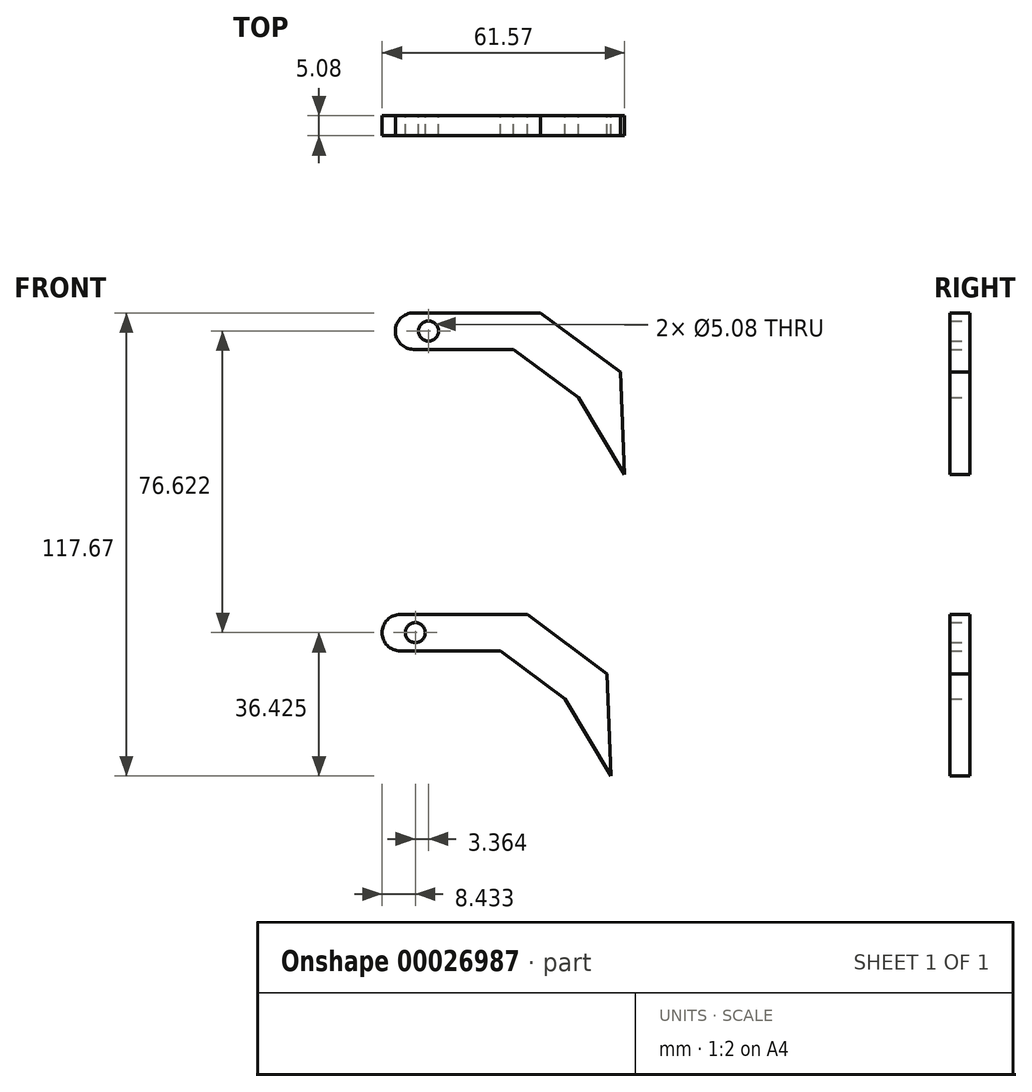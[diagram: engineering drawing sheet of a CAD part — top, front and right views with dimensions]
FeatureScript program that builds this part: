
annotation { "Feature Type Name" : "Feature", "Feature Type Description" : "" }
export const myFeature = defineFeature(function(context is Context, id is Id, definition is map)
    precondition{}
    {
        {
            var Q0;
            Q0=qCreatedBy(makeId("Front.planeOp"),FACE);
            var sketch = newSketch(context, id + "F0", { "sketchPlane" : qUnion([Q0])});
            skLineSegment(sketch, "E0.bottom", {"start": v(-41.86, 34.1) * mm, "end": v(-16.46, 34.1) * mm});
            skLineSegment(sketch, "E0.top", {"start": v(-41.86, 24.85) * mm, "end": v(-16.46, 24.85) * mm});
            skLineSegment(sketch, "E0.left", {"start": v(-41.86, 34.1) * mm, "end": v(-41.86, 24.85) * mm});
            skLineSegment(sketch, "E0.right", {"start": v(-16.46, 34.1) * mm, "end": v(-16.46, 24.85) * mm});
            skLineSegment(sketch, "E1", {"start": v(-16.46, 24.85) * mm, "end": v(-9.59, 34.1) * mm});
            skLineSegment(sketch, "E2", {"start": v(-9.59, 34.1) * mm, "end": v(-16.46, 34.1) * mm});
            skLineSegment(sketch, "E3.top", {"start": v(-16.46, 34.1) * mm, "end": v(-9.59, 34.1) * mm});
            skLineSegment(sketch, "E3.left", {"start": v(-16.46, 24.85) * mm, "end": v(-16.46, 34.1) * mm});
            skPoint(sketch, "E3.right.end.orphan", {"position": v(3.14, 34.1) * mm});
            skLineSegment(sketch, "E4", {"start": v(-16.46, 24.85) * mm, "end": v(0, 12.62) * mm});
            skLineSegment(sketch, "E5", {"start": v(-9.59, 34.1) * mm, "end": v(10.7, 19.03) * mm});
            skLineSegment(sketch, "E6", {"start": v(0, 12.62) * mm, "end": v(10.7, 19.03) * mm});
            skLineSegment(sketch, "E7", {"start": v(0, 12.62) * mm, "end": v(11.72, -6.94) * mm});
            skLineSegment(sketch, "E8", {"start": v(11.72, -6.94) * mm, "end": v(10.7, 19.03) * mm});
            skLineSegment(sketch, "E9", {"start": v(-3.36, -64) * mm, "end": v(7.34, -57.6) * mm});
            skLineSegment(sketch, "E10", {"start": v(-3.36, -64) * mm, "end": v(8.35, -83.57) * mm});
            skLineSegment(sketch, "E11", {"start": v(8.35, -83.57) * mm, "end": v(7.34, -57.6) * mm});
            skPoint(sketch, "E12.right.end.orphan", {"position": v(-0.23, -42.52) * mm});
            skLineSegment(sketch, "E13", {"start": v(-12.95, -42.52) * mm, "end": v(7.34, -57.6) * mm});
            skLineSegment(sketch, "E14", {"start": v(-19.83, -51.77) * mm, "end": v(-3.36, -64) * mm});
            skLineSegment(sketch, "E12.left", {"start": v(-19.83, -51.77) * mm, "end": v(-19.83, -42.52) * mm});
            skLineSegment(sketch, "E15", {"start": v(-19.83, -51.77) * mm, "end": v(-12.95, -42.52) * mm});
            skLineSegment(sketch, "E12.top", {"start": v(-19.83, -42.52) * mm, "end": v(-12.95, -42.52) * mm});
            skLineSegment(sketch, "E16.left", {"start": v(-45.23, -42.52) * mm, "end": v(-45.23, -51.77) * mm});
            skLineSegment(sketch, "E16.top", {"start": v(-45.23, -51.77) * mm, "end": v(-19.83, -51.77) * mm});
            skLineSegment(sketch, "E16.bottom", {"start": v(-45.23, -42.52) * mm, "end": v(-19.83, -42.52) * mm});
            skLineSegment(sketch, "E16.right", {"start": v(-19.83, -42.52) * mm, "end": v(-19.83, -51.77) * mm});
            skLineSegment(sketch, "E17", {"start": v(-12.95, -42.52) * mm, "end": v(-19.83, -42.52) * mm});
            skPoint(sketch, "E18", {"position": v(-41.86, 29.48) * mm});
            skPoint(sketch, "E19", {"position": v(-38.05, 29.48) * mm});
            skCircle(sketch, "E20", {"center": v(-38.05, 29.48) * mm, "radius": 2.54 * mm});
            skPoint(sketch, "E21", {"position": v(-45.23, -47.14) * mm});
            skPoint(sketch, "E22", {"position": v(-41.42, -47.14) * mm});
            skCircle(sketch, "E23", {"center": v(-41.42, -47.14) * mm, "radius": 2.54 * mm});
            skArc(sketch, "E24", {"start": v(-41.86, 34.1) * mm, "mid": v(-46.49, 29.48) * mm, "end": v(-41.86, 24.85) * mm});
            skArc(sketch, "E25", {"start": v(-45.23, -42.52) * mm, "mid": v(-49.85, -47.14) * mm, "end": v(-45.23, -51.77) * mm});
            skSolve(sketch);
        }
        {
            var Q0;
            Q0=makeQuery(id+"F0.imprint","IMPRINT",FACE,{"disambiguationData":[TD([[makeQuery(id+"F0.imprint","IMPRINT",EDGE,{"derivedFrom":sQuery(id+"F0.wireOp",EDGE,"E1")}),1.0]])]});
            var Q1;
            Q1=makeQuery(id+"F0.imprint","IMPRINT",FACE,{"disambiguationData":[TD([[makeQuery(id+"F0.imprint","IMPRINT",EDGE,{"derivedFrom":sQuery(id+"F0.wireOp",EDGE,"E1")}),-1.0]])]});
            var Q2;
            Q2=makeQuery(id+"F0.imprint","IMPRINT",FACE,{"disambiguationData":[TD([[makeQuery(id+"F0.imprint","IMPRINT",EDGE,{"derivedFrom":sQuery(id+"F0.wireOp",EDGE,"E6")}),-1.0]])]});
            var Q3;
            Q3=makeQuery(id+"F0.imprint","IMPRINT",FACE,{"disambiguationData":[TD([[makeQuery(id+"F0.imprint","IMPRINT",EDGE,{"derivedFrom":sQuery(id+"F0.wireOp",EDGE,"E0.bottom")}),-1.0]])]});
            extrude(context, id + "F1", {"entities" : qUnion([Q0, Q1, Q2, Q3]), "depth" : 5.08 * mm});
        }
        {
            var Q0;
            Q0=makeQuery(id+"F0.imprint","IMPRINT",FACE,{"disambiguationData":[TD([[makeQuery(id+"F0.imprint","IMPRINT",EDGE,{"derivedFrom":sQuery(id+"F0.wireOp",EDGE,"E15")}),1.0]])]});
            var Q1;
            Q1=makeQuery(id+"F0.imprint","IMPRINT",FACE,{"disambiguationData":[TD([[makeQuery(id+"F0.imprint","IMPRINT",EDGE,{"derivedFrom":sQuery(id+"F0.wireOp",EDGE,"E9")}),1.0]])]});
            var Q2;
            Q2=makeQuery(id+"F0.imprint","IMPRINT",FACE,{"disambiguationData":[TD([[makeQuery(id+"F0.imprint","IMPRINT",EDGE,{"derivedFrom":sQuery(id+"F0.wireOp",EDGE,"E16.left")}),1.0]])]});
            var Q3;
            Q3=makeQuery(id+"F0.imprint","IMPRINT",FACE,{"disambiguationData":[TD([[makeQuery(id+"F0.imprint","IMPRINT",EDGE,{"derivedFrom":sQuery(id+"F0.wireOp",EDGE,"E9")}),-1.0]])]});
            extrude(context, id + "F2", {"entities" : qUnion([Q0, Q1, Q2, Q3]), "depth" : 5.08 * mm});
        }
        {
            var Q0;
            Q0=makeQuery(id+"F0.imprint","IMPRINT",FACE,{"disambiguationData":[TD([[makeQuery(id+"F0.imprint","IMPRINT",EDGE,{"derivedFrom":sQuery(id+"F0.wireOp",EDGE,"E0.left")}),-1.0]])]});
            extrude(context, id + "F3", {"entities" : qUnion([Q0]), "operationType" : NewBodyOperationType.ADD, "depth" : 5.08 * mm});
        }
        {
            var Q0;
            Q0=makeQuery(id+"F0.imprint","IMPRINT",FACE,{"disambiguationData":[TD([[makeQuery(id+"F0.imprint","IMPRINT",EDGE,{"derivedFrom":sQuery(id+"F0.wireOp",EDGE,"E16.left")}),-1.0]])]});
            extrude(context, id + "F4", {"entities" : qUnion([Q0]), "operationType" : NewBodyOperationType.ADD, "depth" : 5.08 * mm});
        }
    });
